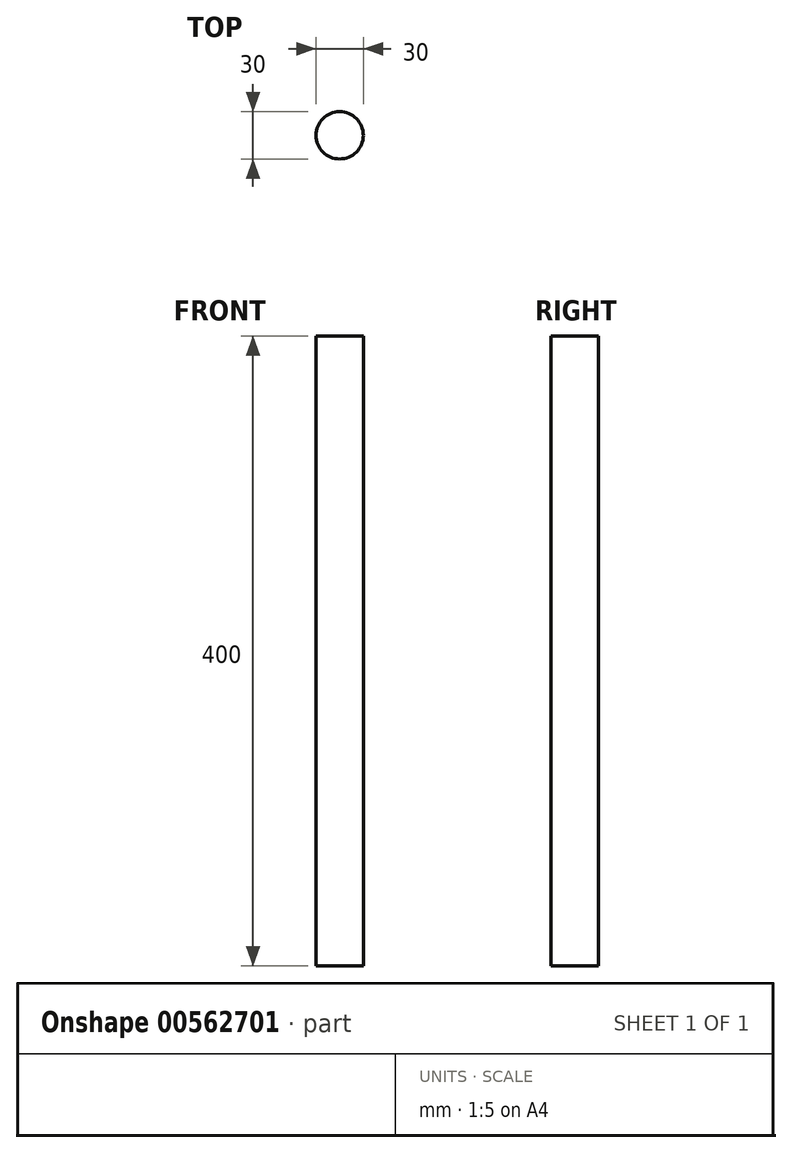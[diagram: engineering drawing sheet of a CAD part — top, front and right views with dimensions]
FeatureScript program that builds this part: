
annotation { "Feature Type Name" : "Feature", "Feature Type Description" : "" }
export const myFeature = defineFeature(function(context is Context, id is Id, definition is map)
    precondition{}
    {
        {
            var Q0;
            Q0=qCreatedBy(makeId("Top.planeOp"),FACE);
            var sketch = newSketch(context, id + "F0", { "sketchPlane" : qUnion([Q0])});
            skCircle(sketch, "E0", {"center": v(0, 0) * mm, "radius": 15 * mm});
            skSolve(sketch);
        }
        {
            var Q0;
            Q0 = qSketchRegion(id + "F0", true);
            extrude(context, id + "F1", {"entities" : qUnion([Q0]), "depth" : 400 * mm, "offsetDistance" : 25.4 * mm});
        }
    });
